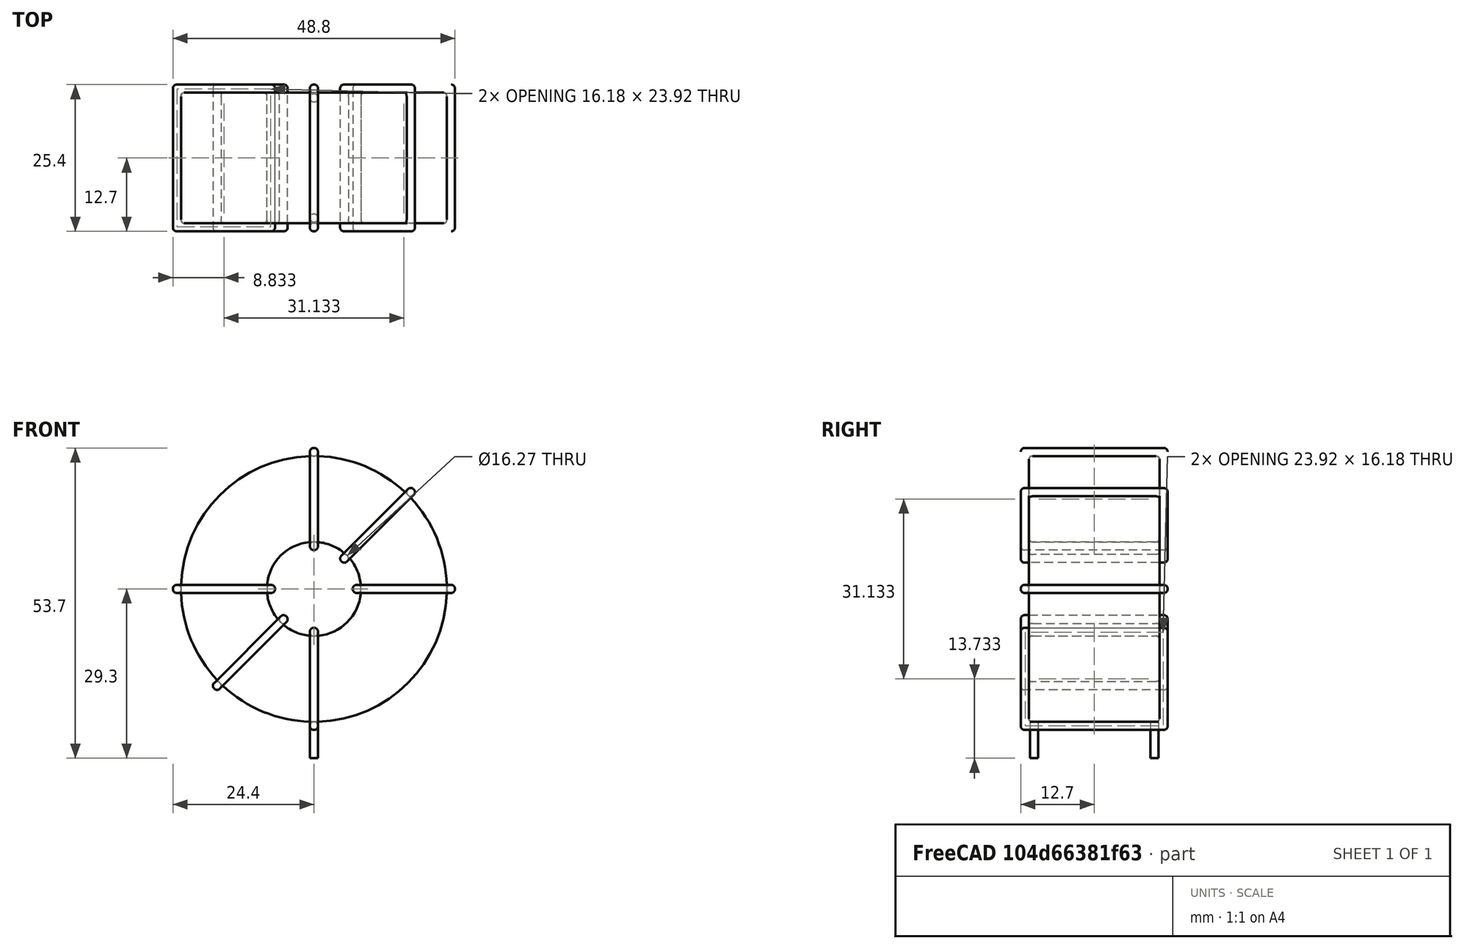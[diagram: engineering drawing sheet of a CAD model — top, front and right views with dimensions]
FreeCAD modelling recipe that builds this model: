
FCSTD DOCUMENT  (FreeCAD 0.16R6703 (Git))
Label: L_Toroid_Vertical_L48.8mm_W25.4mm_P20.80mm_Vishay_TJ8
License: All rights reserved
LicenseURL: http://en.wikipedia.org/wiki/All_rights_reserved
objects: Sketcher::SketchObject×6, PartDesign::Pad×6, PartDesign::Fillet×5, Spreadsheet::Sheet×1
note: 23 computed .brp shape members not serialized (recipe doc carries the construction recipe); baked Part::Feature solids carry a one-line shape summary decoded from their .brp

FEATURE [Spreadsheet::Sheet] Spreadsheet  label="dimensions"
  cells = A1=Wx; B1(Wx)=48.8; C1(WW)=16.26666666666667; D1=48.8; A2=Wy; B2(Wy)=25.4; D2=25.4; A3=RM; B3(RMx)=20.8; C3(RMy)=0; A4=d_wire; B4(d_wire)=1.4; A5=H; B5(H)=48.8; A6=offsetx; B6(offsetx)=24.4
FEATURE [Sketcher::SketchObject] Sketch
  Placement = pos=(0,-10.4,0) rot=(1,0,0;1.5708rad)
  expr: Placement.Base.y = -Spreadsheet.RMx / 2
  expr: Constraints[0] = Spreadsheet.Wx / 2 - Spreadsheet.d_wire
  expr: Constraints[4] = Spreadsheet.WW / 2
  expr: Constraints[2] = Spreadsheet.Wx / 2 + Spreadsheet.d_wire + 0.5
  sketch-geometry (2):
    g0: Circle CenterX=0 CenterY=26.3 CenterZ=0 NormalX=0 NormalY=0 NormalZ=1 Radius=23
    g1: Circle CenterX=0 CenterY=26.3 CenterZ=0 NormalX=0 NormalY=0 NormalZ=1 Radius=8.13333
  constraints (5):
    c: Radius(g0) = 23
    c: DistanceX(g-1,g0) = 0
    c: DistanceY(g-1,g0) = 26.3
    c: Coincident(g1,g0)
    c: Radius(g1) = 8.13333
FEATURE [PartDesign::Pad] Pad
  Length = 22.6
  Length2 = 100
  Midplane = true
  Placement = pos=(0,-10.4,0) rot=(1,0,0;1.5708rad)
  Sketch = -> Sketch
  Type = 0
  expr: Length = Spreadsheet.Wy - 2 * Spreadsheet.d_wire
FEATURE [Sketcher::SketchObject] Sketch001
  Placement = pos=(0,0,1.9) rot=(0,0,1;0rad)
  expr: Placement.Base.z = 0.5 + Spreadsheet.d_wire
  expr: Constraints[4] = Spreadsheet.RMy
  expr: Constraints[2] = -Spreadsheet.RMx
  expr: Constraints[1] = Spreadsheet.d_wire / 2
  sketch-geometry (2):
    g0: Circle CenterX=0 CenterY=0 CenterZ=0 NormalX=0 NormalY=0 NormalZ=1 Radius=0.7
    g1: Circle CenterX=0 CenterY=-20.8 CenterZ=0 NormalX=0 NormalY=0 NormalZ=1 Radius=0.7
  constraints (5):
    c: Equal(g0,g1)
    c: Radius(g0) = 0.7
    c: DistanceY(g-1,g1) = -20.8
    c: Coincident(g0,g-1)
    c: DistanceX(g-1,g1) = 0
FEATURE [PartDesign::Pad] Pad001
  Length = 1.4
  Length2 = 4.9
  Placement = pos=(0,0,1.9) rot=(0,0,1;0rad)
  Reversed = true
  Sketch = -> Sketch001
  Type = 4
  expr: Length2 = 3.5 + Spreadsheet.d_wire
  expr: Length = Spreadsheet.d_wire
FEATURE [PartDesign::Fillet] Fillet
  Base = -> Pad [Edge6,Edge3,Edge2]
  Placement = pos=(0,-10.4,0) rot=(1,0,0;1.5708rad)
  Radius = 0.5
FEATURE [Sketcher::SketchObject] Sketch003
  Placement = pos=(0,2.3,26.3) rot=(1,0,0;3.14159rad)
  expr: Constraints[18] = Spreadsheet.d_wire
  expr: Constraints[16] = Spreadsheet.d_wire
  expr: Constraints[19] = Spreadsheet.d_wire
  expr: Constraints[17] = Spreadsheet.d_wire
  expr: Placement.Base.y = -1 * (Spreadsheet.RMx - Spreadsheet.Wy) / 2
  expr: Constraints[21] = (Spreadsheet.Wx - Spreadsheet.WW) / 2 - Spreadsheet.d_wire
  expr: Constraints[22] = Spreadsheet.Wx / 2 - Spreadsheet.d_wire
  expr: Constraints[43] = Spreadsheet.d_wire
  expr: Constraints[48] = Spreadsheet.Wx - Spreadsheet.d_wire * 2
  expr: Constraints[49] = Spreadsheet.Wy
  expr: Placement.Base.z = Spreadsheet.Wx / 2 + Spreadsheet.d_wire + 0.5
  sketch-geometry (16):
    g0: LineSegment StartX=-6.73333 StartY=0 StartZ=0 EndX=-24.4 EndY=0 EndZ=0
    g1: LineSegment StartX=-24.4 StartY=0 StartZ=0 EndX=-24.4 EndY=25.4 EndZ=0
    g2: LineSegment StartX=-24.4 StartY=25.4 StartZ=0 EndX=-6.73333 EndY=25.4 EndZ=0
    g3: LineSegment StartX=-6.73333 StartY=25.4 StartZ=0 EndX=-6.73333 EndY=0 EndZ=0
    g4: LineSegment StartX=-23 StartY=24 StartZ=0 EndX=-8.13333 EndY=24 EndZ=0
    g5: LineSegment StartX=-8.13333 StartY=24 StartZ=0 EndX=-8.13333 EndY=1.4 EndZ=0
    g6: LineSegment StartX=-8.13333 StartY=1.4 StartZ=0 EndX=-23 EndY=1.4 EndZ=0
    g7: LineSegment StartX=-23 StartY=1.4 StartZ=0 EndX=-23 EndY=24 EndZ=0
    g8: LineSegment StartX=6.73333 StartY=25.4 StartZ=0 EndX=24.4 EndY=25.4 EndZ=0
    g9: LineSegment StartX=24.4 StartY=25.4 StartZ=0 EndX=24.4 EndY=0 EndZ=0
    g10: LineSegment StartX=24.4 StartY=0 StartZ=0 EndX=6.73333 EndY=0 EndZ=0
    g11: LineSegment StartX=6.73333 StartY=0 StartZ=0 EndX=6.73333 EndY=25.4 EndZ=0
    g12: LineSegment StartX=8.13333 StartY=24 StartZ=0 EndX=23 EndY=24 EndZ=0
    g13: LineSegment StartX=23 StartY=24 StartZ=0 EndX=23 EndY=1.4 EndZ=0
    g14: LineSegment StartX=23 StartY=1.4 StartZ=0 EndX=8.13333 EndY=1.4 EndZ=0
    g15: LineSegment StartX=8.13333 StartY=1.4 StartZ=0 EndX=8.13333 EndY=24 EndZ=0
  constraints (50):
    c: Horizontal(g0)
    c: Coincident(g1,g0)
    c: Vertical(g1)
    c: Coincident(g2,g1)
    c: Horizontal(g2)
    c: Coincident(g3,g2)
    c: Coincident(g3,g0)
    c: Vertical(g3)
    c: Coincident(g4,g5)
    c: Coincident(g5,g6)
    c: Coincident(g6,g7)
    c: Coincident(g7,g4)
    c: Horizontal(g4)
    c: Horizontal(g6)
    c: Vertical(g5)
    c: Vertical(g7)
    c: DistanceX(g1,g4) = 1.4
    c: DistanceY(g4,g1) = 1.4
    c: DistanceX(g5,g0) = 1.4
    c: DistanceY(g0,g5) = 1.4
    c: DistanceY(g-1,g0) = 0
    c: DistanceX(g6,g6) = 14.8667
    c: DistanceX(g6,g-1) = 23
    c: Coincident(g8,g9)
    c: Coincident(g9,g10)
    c: Coincident(g10,g11)
    c: Coincident(g11,g8)
    c: Horizontal(g8)
    c: Horizontal(g10)
    c: Vertical(g9)
    c: Vertical(g11)
    c: Coincident(g12,g13)
    c: Coincident(g13,g14)
    c: Coincident(g14,g15)
    c: Coincident(g15,g12)
    c: Horizontal(g12)
    c: Horizontal(g14)
    c: Vertical(g13)
    c: Vertical(g15)
    c: DistanceY(g8,g2) = 0
    c: DistanceY(g10,g0) = 0
    c: DistanceY(g14,g5) = 0
    c: DistanceY(g12,g4) = 0
    c: DistanceX(g8,g12) = 1.4
    c: Equal(g8,g2)
    c: Equal(g12,g4)
    c: Equal(g9,g1)
    c: Equal(g13,g7)
    c: DistanceX(g4,g12) = 46
    c: DistanceY(g0,g1) = 25.4
FEATURE [PartDesign::Pad] Pad002
  Length = 1.4
  Length2 = 100
  Midplane = true
  Placement = pos=(0,2.3,26.3) rot=(1,0,0;3.14159rad)
  Sketch = -> Sketch003
  Type = 0
  expr: Length = Spreadsheet.d_wire
FEATURE [PartDesign::Fillet] Fillet001
  Base = -> Pad002 [Edge38,Edge41,Edge42,Edge43,Edge29,Edge32,Edge33,Edge34,Edge25,Edge35,Edge36,Edge13,Edge14,Edge15,Edge16,Edge17,Edge18,Edge19,Edge1,Edge2,Edge3,Edge4,Edge5,Edge6,Edge7,Edge37,Edge39,Edge40,Edge20,Edge23,Edge24,Edge21,Edge22,Edge8,Edge9,Edge10,Edge11,Edge12,Edge26,Edge27,+8 more]
  Placement = pos=(0,2.3,26.3) rot=(1,0,0;3.14159rad)
  Radius = 0.658
  expr: Radius = Spreadsheet.d_wire * 0.47
FEATURE [Sketcher::SketchObject] Sketch004
  Placement = pos=(0,2.3,26.3) rot=(0.92388,0,0.382683;3.14159rad)
  expr: Constraints[18] = Spreadsheet.d_wire
  expr: Constraints[16] = Spreadsheet.d_wire
  expr: Constraints[19] = Spreadsheet.d_wire
  expr: Constraints[17] = Spreadsheet.d_wire
  expr: Placement.Base.y = -1 * (Spreadsheet.RMx - Spreadsheet.Wy) / 2
  expr: Constraints[21] = (Spreadsheet.Wx - Spreadsheet.WW) / 2 - Spreadsheet.d_wire
  expr: Constraints[22] = Spreadsheet.Wx / 2 - Spreadsheet.d_wire
  expr: Constraints[43] = Spreadsheet.d_wire
  expr: Constraints[48] = Spreadsheet.Wx - 2 * Spreadsheet.d_wire
  expr: Constraints[49] = Spreadsheet.Wy
  expr: Placement.Base.z = Spreadsheet.Wx / 2 + Spreadsheet.d_wire + 0.5
  sketch-geometry (16):
    g0: LineSegment StartX=-6.73333 StartY=0 StartZ=0 EndX=-24.4 EndY=0 EndZ=0
    g1: LineSegment StartX=-24.4 StartY=0 StartZ=0 EndX=-24.4 EndY=25.4 EndZ=0
    g2: LineSegment StartX=-24.4 StartY=25.4 StartZ=0 EndX=-6.73333 EndY=25.4 EndZ=0
    g3: LineSegment StartX=-6.73333 StartY=25.4 StartZ=0 EndX=-6.73333 EndY=0 EndZ=0
    g4: LineSegment StartX=-23 StartY=24 StartZ=0 EndX=-8.13333 EndY=24 EndZ=0
    g5: LineSegment StartX=-8.13333 StartY=24 StartZ=0 EndX=-8.13333 EndY=1.4 EndZ=0
    g6: LineSegment StartX=-8.13333 StartY=1.4 StartZ=0 EndX=-23 EndY=1.4 EndZ=0
    g7: LineSegment StartX=-23 StartY=1.4 StartZ=0 EndX=-23 EndY=24 EndZ=0
    g8: LineSegment StartX=6.73333 StartY=25.4 StartZ=0 EndX=24.4 EndY=25.4 EndZ=0
    g9: LineSegment StartX=24.4 StartY=25.4 StartZ=0 EndX=24.4 EndY=0 EndZ=0
    g10: LineSegment StartX=24.4 StartY=0 StartZ=0 EndX=6.73333 EndY=0 EndZ=0
    g11: LineSegment StartX=6.73333 StartY=0 StartZ=0 EndX=6.73333 EndY=25.4 EndZ=0
    g12: LineSegment StartX=8.13333 StartY=24 StartZ=0 EndX=23 EndY=24 EndZ=0
    g13: LineSegment StartX=23 StartY=24 StartZ=0 EndX=23 EndY=1.4 EndZ=0
    g14: LineSegment StartX=23 StartY=1.4 StartZ=0 EndX=8.13333 EndY=1.4 EndZ=0
    g15: LineSegment StartX=8.13333 StartY=1.4 StartZ=0 EndX=8.13333 EndY=24 EndZ=0
  constraints (50):
    c: Horizontal(g0)
    c: Coincident(g1,g0)
    c: Vertical(g1)
    c: Coincident(g2,g1)
    c: Horizontal(g2)
    c: Coincident(g3,g2)
    c: Coincident(g3,g0)
    c: Vertical(g3)
    c: Coincident(g4,g5)
    c: Coincident(g5,g6)
    c: Coincident(g6,g7)
    c: Coincident(g7,g4)
    c: Horizontal(g4)
    c: Horizontal(g6)
    c: Vertical(g5)
    c: Vertical(g7)
    c: DistanceX(g1,g4) = 1.4
    c: DistanceY(g4,g1) = 1.4
    c: DistanceX(g5,g0) = 1.4
    c: DistanceY(g0,g5) = 1.4
    c: DistanceY(g-1,g0) = 0
    c: DistanceX(g6,g6) = 14.8667
    c: DistanceX(g6,g-1) = 23
    c: Coincident(g8,g9)
    c: Coincident(g9,g10)
    c: Coincident(g10,g11)
    c: Coincident(g11,g8)
    c: Horizontal(g8)
    c: Horizontal(g10)
    c: Vertical(g9)
    c: Vertical(g11)
    c: Coincident(g12,g13)
    c: Coincident(g13,g14)
    c: Coincident(g14,g15)
    c: Coincident(g15,g12)
    c: Horizontal(g12)
    c: Horizontal(g14)
    c: Vertical(g13)
    c: Vertical(g15)
    c: DistanceY(g8,g2) = 0
    c: DistanceY(g10,g0) = 0
    c: DistanceY(g14,g5) = 0
    c: DistanceY(g12,g4) = 0
    c: DistanceX(g8,g12) = 1.4
    c: Equal(g8,g2)
    c: Equal(g12,g4)
    c: Equal(g9,g1)
    c: Equal(g13,g7)
    c: DistanceX(g4,g12) = 46
    c: DistanceY(g0,g1) = 25.4
FEATURE [PartDesign::Pad] Pad003
  Length = 1.4
  Length2 = 100
  Midplane = true
  Placement = pos=(0,2.3,26.3) rot=(0.92388,0,0.382683;3.14159rad)
  Sketch = -> Sketch004
  Type = 0
  expr: Length = Spreadsheet.d_wire
FEATURE [PartDesign::Fillet] Fillet002
  Base = -> Pad003 [Edge38,Edge41,Edge42,Edge43,Edge29,Edge32,Edge33,Edge34,Edge25,Edge35,Edge36,Edge13,Edge14,Edge15,Edge16,Edge17,Edge18,Edge19,Edge1,Edge2,Edge3,Edge4,Edge5,Edge6,Edge7,Edge37,Edge39,Edge40,Edge20,Edge23,Edge24,Edge21,Edge22,Edge8,Edge9,Edge10,Edge11,Edge12,Edge26,Edge27,+8 more]
  Placement = pos=(0,2.3,26.3) rot=(0.92388,0,0.382683;3.14159rad)
  Radius = 0.658
  expr: Radius = Spreadsheet.d_wire * 0.47
FEATURE [Sketcher::SketchObject] Sketch005
  Placement = pos=(0,2.3,26.3) rot=(0.92388,0,-0.382683;3.14159rad)
  expr: Constraints[18] = Spreadsheet.d_wire
  expr: Constraints[16] = Spreadsheet.d_wire
  expr: Constraints[19] = Spreadsheet.d_wire
  expr: Constraints[17] = Spreadsheet.d_wire
  expr: Placement.Base.y = -1 * (Spreadsheet.RMx - Spreadsheet.Wy) / 2
  expr: Constraints[21] = (Spreadsheet.Wx - Spreadsheet.WW) / 2 - Spreadsheet.d_wire
  expr: Constraints[22] = Spreadsheet.Wx / 2 - Spreadsheet.d_wire
  expr: Constraints[43] = Spreadsheet.d_wire
  expr: Constraints[48] = Spreadsheet.Wx - 2 * Spreadsheet.d_wire
  expr: Constraints[49] = Spreadsheet.Wy
  expr: Placement.Base.z = Spreadsheet.Wx / 2 + Spreadsheet.d_wire + 0.5
  sketch-geometry (16):
    g0: LineSegment StartX=-6.73333 StartY=0 StartZ=0 EndX=-24.4 EndY=0 EndZ=0
    g1: LineSegment StartX=-24.4 StartY=0 StartZ=0 EndX=-24.4 EndY=25.4 EndZ=0
    g2: LineSegment StartX=-24.4 StartY=25.4 StartZ=0 EndX=-6.73333 EndY=25.4 EndZ=0
    g3: LineSegment StartX=-6.73333 StartY=25.4 StartZ=0 EndX=-6.73333 EndY=0 EndZ=0
    g4: LineSegment StartX=-23 StartY=24 StartZ=0 EndX=-8.13333 EndY=24 EndZ=0
    g5: LineSegment StartX=-8.13333 StartY=24 StartZ=0 EndX=-8.13333 EndY=1.4 EndZ=0
    g6: LineSegment StartX=-8.13333 StartY=1.4 StartZ=0 EndX=-23 EndY=1.4 EndZ=0
    g7: LineSegment StartX=-23 StartY=1.4 StartZ=0 EndX=-23 EndY=24 EndZ=0
    g8: LineSegment StartX=6.73333 StartY=25.4 StartZ=0 EndX=24.4 EndY=25.4 EndZ=0
    g9: LineSegment StartX=24.4 StartY=25.4 StartZ=0 EndX=24.4 EndY=0 EndZ=0
    g10: LineSegment StartX=24.4 StartY=0 StartZ=0 EndX=6.73333 EndY=0 EndZ=0
    g11: LineSegment StartX=6.73333 StartY=0 StartZ=0 EndX=6.73333 EndY=25.4 EndZ=0
    g12: LineSegment StartX=8.13333 StartY=24 StartZ=0 EndX=23 EndY=24 EndZ=0
    g13: LineSegment StartX=23 StartY=24 StartZ=0 EndX=23 EndY=1.4 EndZ=0
    g14: LineSegment StartX=23 StartY=1.4 StartZ=0 EndX=8.13333 EndY=1.4 EndZ=0
    g15: LineSegment StartX=8.13333 StartY=1.4 StartZ=0 EndX=8.13333 EndY=24 EndZ=0
  constraints (50):
    c: Horizontal(g0)
    c: Coincident(g1,g0)
    c: Vertical(g1)
    c: Coincident(g2,g1)
    c: Horizontal(g2)
    c: Coincident(g3,g2)
    c: Coincident(g3,g0)
    c: Vertical(g3)
    c: Coincident(g4,g5)
    c: Coincident(g5,g6)
    c: Coincident(g6,g7)
    c: Coincident(g7,g4)
    c: Horizontal(g4)
    c: Horizontal(g6)
    c: Vertical(g5)
    c: Vertical(g7)
    c: DistanceX(g1,g4) = 1.4
    c: DistanceY(g4,g1) = 1.4
    c: DistanceX(g5,g0) = 1.4
    c: DistanceY(g0,g5) = 1.4
    c: DistanceY(g-1,g0) = 0
    c: DistanceX(g6,g6) = 14.8667
    c: DistanceX(g6,g-1) = 23
    c: Coincident(g8,g9)
    c: Coincident(g9,g10)
    c: Coincident(g10,g11)
    c: Coincident(g11,g8)
    c: Horizontal(g8)
    c: Horizontal(g10)
    c: Vertical(g9)
    c: Vertical(g11)
    c: Coincident(g12,g13)
    c: Coincident(g13,g14)
    c: Coincident(g14,g15)
    c: Coincident(g15,g12)
    c: Horizontal(g12)
    c: Horizontal(g14)
    c: Vertical(g13)
    c: Vertical(g15)
    c: DistanceY(g8,g2) = 0
    c: DistanceY(g10,g0) = 0
    c: DistanceY(g14,g5) = 0
    c: DistanceY(g12,g4) = 0
    c: DistanceX(g8,g12) = 1.4
    c: Equal(g8,g2)
    c: Equal(g12,g4)
    c: Equal(g9,g1)
    c: Equal(g13,g7)
    c: DistanceX(g4,g12) = 46
    c: DistanceY(g0,g1) = 25.4
FEATURE [PartDesign::Pad] Pad004
  Length = 1.4
  Length2 = 100
  Midplane = true
  Placement = pos=(0,2.3,26.3) rot=(0.92388,0,-0.382683;3.14159rad)
  Sketch = -> Sketch005
  Type = 0
  expr: Length = Spreadsheet.d_wire
FEATURE [PartDesign::Fillet] Fillet003
  Base = -> Pad004 [Edge38,Edge41,Edge42,Edge43,Edge29,Edge32,Edge33,Edge34,Edge25,Edge35,Edge36,Edge13,Edge14,Edge15,Edge16,Edge17,Edge18,Edge19,Edge1,Edge2,Edge3,Edge4,Edge5,Edge6,Edge7,Edge37,Edge39,Edge40,Edge20,Edge23,Edge24,Edge21,Edge22,Edge8,Edge9,Edge10,Edge11,Edge12,Edge26,Edge27,+8 more]
  Placement = pos=(0,2.3,26.3) rot=(0.92388,0,-0.382683;3.14159rad)
  Radius = 0.658
  expr: Radius = Spreadsheet.d_wire * 0.47
FEATURE [Sketcher::SketchObject] Sketch006
  Placement = pos=(0,2.3,26.3) rot=(0.707107,0,0.707107;3.14159rad)
  expr: Constraints[18] = Spreadsheet.d_wire
  expr: Constraints[16] = Spreadsheet.d_wire
  expr: Constraints[19] = Spreadsheet.d_wire
  expr: Constraints[17] = Spreadsheet.d_wire
  expr: Placement.Base.y = -1 * (Spreadsheet.RMx - Spreadsheet.Wy) / 2
  expr: Constraints[21] = (Spreadsheet.Wx - Spreadsheet.WW) / 2 - Spreadsheet.d_wire
  expr: Constraints[22] = Spreadsheet.Wx / 2 - Spreadsheet.d_wire
  expr: Constraints[43] = Spreadsheet.d_wire
  expr: Constraints[48] = Spreadsheet.Wx - Spreadsheet.d_wire * 2
  expr: Constraints[49] = Spreadsheet.Wy
  expr: Placement.Base.z = Spreadsheet.Wx / 2 + Spreadsheet.d_wire + 0.5
  sketch-geometry (16):
    g0: LineSegment StartX=-6.73333 StartY=0 StartZ=0 EndX=-24.4 EndY=0 EndZ=0
    g1: LineSegment StartX=-24.4 StartY=0 StartZ=0 EndX=-24.4 EndY=25.4 EndZ=0
    g2: LineSegment StartX=-24.4 StartY=25.4 StartZ=0 EndX=-6.73333 EndY=25.4 EndZ=0
    g3: LineSegment StartX=-6.73333 StartY=25.4 StartZ=0 EndX=-6.73333 EndY=0 EndZ=0
    g4: LineSegment StartX=-23 StartY=24 StartZ=0 EndX=-8.13333 EndY=24 EndZ=0
    g5: LineSegment StartX=-8.13333 StartY=24 StartZ=0 EndX=-8.13333 EndY=1.4 EndZ=0
    g6: LineSegment StartX=-8.13333 StartY=1.4 StartZ=0 EndX=-23 EndY=1.4 EndZ=0
    g7: LineSegment StartX=-23 StartY=1.4 StartZ=0 EndX=-23 EndY=24 EndZ=0
    g8: LineSegment StartX=6.73333 StartY=25.4 StartZ=0 EndX=24.4 EndY=25.4 EndZ=0
    g9: LineSegment StartX=24.4 StartY=25.4 StartZ=0 EndX=24.4 EndY=0 EndZ=0
    g10: LineSegment StartX=24.4 StartY=0 StartZ=0 EndX=6.73333 EndY=0 EndZ=0
    g11: LineSegment StartX=6.73333 StartY=0 StartZ=0 EndX=6.73333 EndY=25.4 EndZ=0
    g12: LineSegment StartX=8.13333 StartY=24 StartZ=0 EndX=23 EndY=24 EndZ=0
    g13: LineSegment StartX=23 StartY=24 StartZ=0 EndX=23 EndY=1.4 EndZ=0
    g14: LineSegment StartX=23 StartY=1.4 StartZ=0 EndX=8.13333 EndY=1.4 EndZ=0
    g15: LineSegment StartX=8.13333 StartY=1.4 StartZ=0 EndX=8.13333 EndY=24 EndZ=0
  constraints (50):
    c: Horizontal(g0)
    c: Coincident(g1,g0)
    c: Vertical(g1)
    c: Coincident(g2,g1)
    c: Horizontal(g2)
    c: Coincident(g3,g2)
    c: Coincident(g3,g0)
    c: Vertical(g3)
    c: Coincident(g4,g5)
    c: Coincident(g5,g6)
    c: Coincident(g6,g7)
    c: Coincident(g7,g4)
    c: Horizontal(g4)
    c: Horizontal(g6)
    c: Vertical(g5)
    c: Vertical(g7)
    c: DistanceX(g1,g4) = 1.4
    c: DistanceY(g4,g1) = 1.4
    c: DistanceX(g5,g0) = 1.4
    c: DistanceY(g0,g5) = 1.4
    c: DistanceY(g-1,g0) = 0
    c: DistanceX(g6,g6) = 14.8667
    c: DistanceX(g6,g-1) = 23
    c: Coincident(g8,g9)
    c: Coincident(g9,g10)
    c: Coincident(g10,g11)
    c: Coincident(g11,g8)
    c: Horizontal(g8)
    c: Horizontal(g10)
    c: Vertical(g9)
    c: Vertical(g11)
    c: Coincident(g12,g13)
    c: Coincident(g13,g14)
    c: Coincident(g14,g15)
    c: Coincident(g15,g12)
    c: Horizontal(g12)
    c: Horizontal(g14)
    c: Vertical(g13)
    c: Vertical(g15)
    c: DistanceY(g8,g2) = 0
    c: DistanceY(g10,g0) = 0
    c: DistanceY(g14,g5) = 0
    c: DistanceY(g12,g4) = 0
    c: DistanceX(g8,g12) = 1.4
    c: Equal(g8,g2)
    c: Equal(g12,g4)
    c: Equal(g9,g1)
    c: Equal(g13,g7)
    c: DistanceX(g4,g12) = 46
    c: DistanceY(g0,g1) = 25.4
FEATURE [PartDesign::Pad] Pad005
  Length = 1.4
  Length2 = 100
  Midplane = true
  Placement = pos=(0,2.3,26.3) rot=(0.707107,0,0.707107;3.14159rad)
  Sketch = -> Sketch006
  Type = 0
  expr: Length = Spreadsheet.d_wire
FEATURE [PartDesign::Fillet] Fillet004
  Base = -> Pad005 [Edge38,Edge41,Edge42,Edge43,Edge29,Edge32,Edge33,Edge34,Edge25,Edge35,Edge36,Edge13,Edge14,Edge15,Edge16,Edge17,Edge18,Edge19,Edge1,Edge2,Edge3,Edge4,Edge5,Edge6,Edge7,Edge37,Edge39,Edge40,Edge20,Edge23,Edge24,Edge21,Edge22,Edge8,Edge9,Edge10,Edge11,Edge12,Edge26,Edge27,+8 more]
  Placement = pos=(0,2.3,26.3) rot=(0.707107,0,0.707107;3.14159rad)
  Radius = 0.658
  expr: Radius = Spreadsheet.d_wire * 0.47
